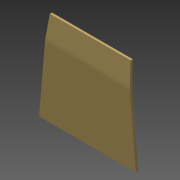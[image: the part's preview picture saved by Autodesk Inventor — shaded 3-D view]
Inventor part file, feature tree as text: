
AUTODESK INVENTOR PART (.ipt)
format: ipt  version: 2015 (Build 190159000, 159)  size: 108,544 bytes
history: native  units: mm
features: other x3, sketch x3, loft x1
ambient origin geometry x8: Origin, YZ Plane, XZ Plane, XY Plane, X Axis, Y Axis, Z Axis, Center Point
bodies: Body1 (feature_tree)
feature tree (7):
  other  "Bryła2"
  sketch  "Szkic1"
  other  "Płaszczyzna konstrukcyjna2"
  loft  "Wyciągnięcie złożone1"
  other  "Gięcie części1"
  sketch  "Szkic3"
  sketch  "Szkic4"
